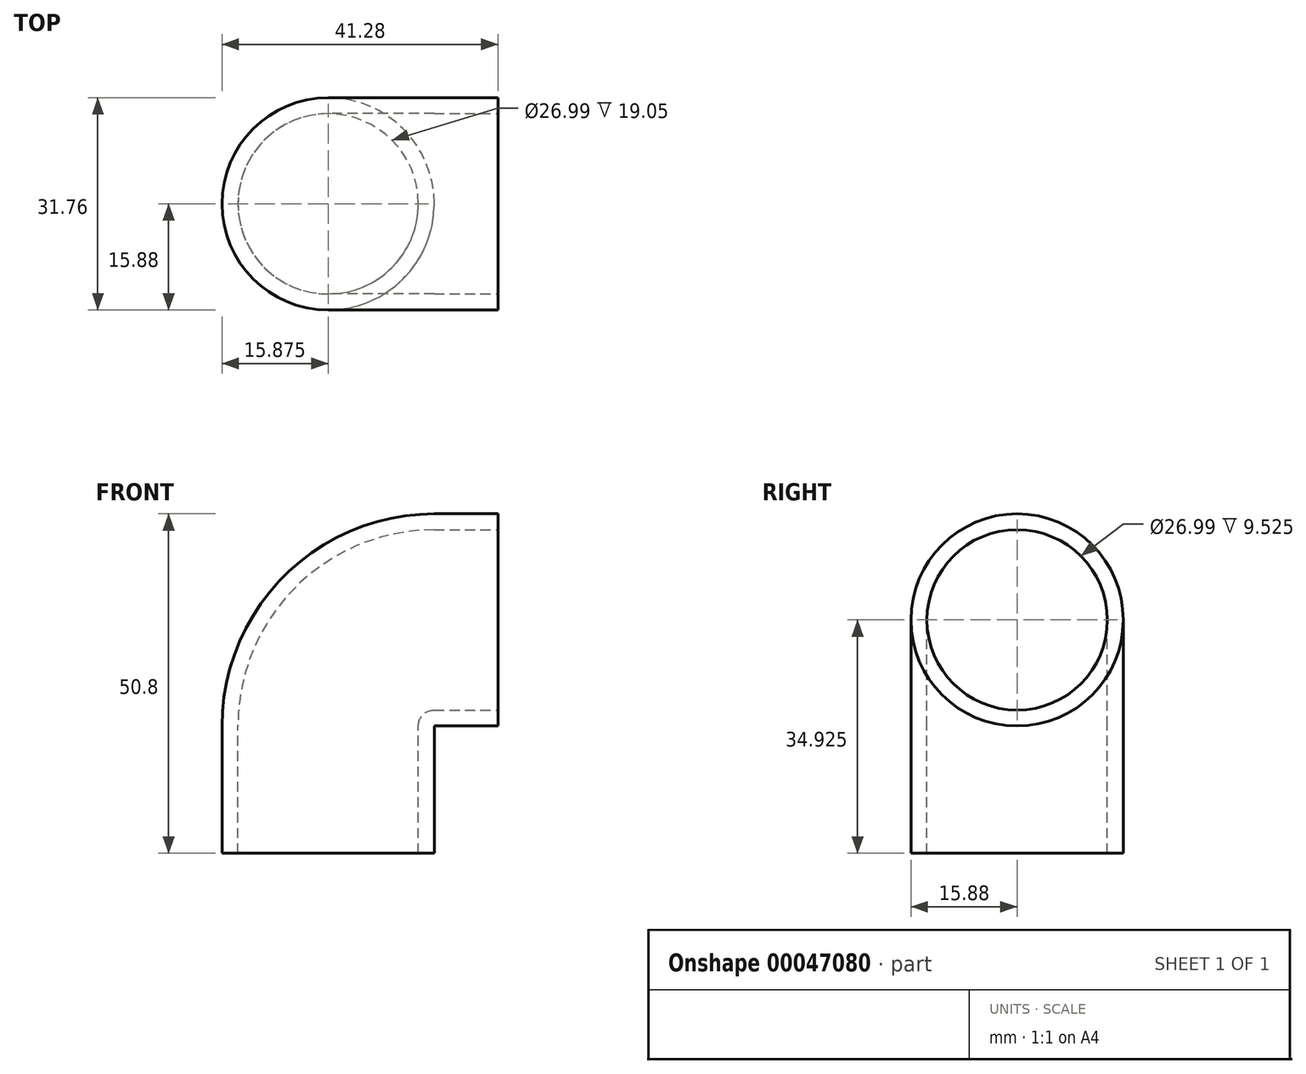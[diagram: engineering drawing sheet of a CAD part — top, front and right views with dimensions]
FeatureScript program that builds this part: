
annotation { "Feature Type Name" : "Feature", "Feature Type Description" : "" }
export const myFeature = defineFeature(function(context is Context, id is Id, definition is map)
    precondition{}
    {
        {
            var Q0;
            Q0=qCreatedBy(makeId("Front.planeOp"),FACE);
            var sketch = newSketch(context, id + "F0", { "sketchPlane" : qUnion([Q0])});
            skLineSegment(sketch, "E0", {"start": v(0, 0) * mm, "end": v(0, 19.05) * mm});
            skLineSegment(sketch, "E1", {"start": v(31.75, 50.8) * mm, "end": v(50.8, 50.8) * mm});
            skPoint(sketch, "E2.visualSharp", {"position": v(0, 50.8) * mm});
            skArc(sketch, "E2.filletArc", {"start": v(31.75, 50.8) * mm, "mid": v(9.3, 41.5) * mm, "end": v(0, 19.05) * mm});
            skSolve(sketch);
        }
        {
            var Q0;
            Q0=qCreatedBy(makeId("Top.planeOp"),FACE);
            var sketch = newSketch(context, id + "F1", { "sketchPlane" : qUnion([Q0])});
            skCircle(sketch, "E3", {"center": v(15.88, 0) * mm, "radius": 15.88 * mm});
            skCircle(sketch, "E4", {"center": v(15.88, 0) * mm, "radius": 13.5 * mm});
            skSolve(sketch);
        }
        {
            var Q0;
            Q0=makeQuery(id+"F1.imprint","IMPRINT",FACE,{"disambiguationData":[TD([[makeQuery(id+"F1.imprint","IMPRINT",EDGE,{"derivedFrom":sQuery(id+"F1.wireOp",EDGE,"E3")}),1.0]])]});
            var Q1;
            Q1=sQuery(id+"F0.wireOp",EDGE,"E0");
            var Q2;
            Q2=sQuery(id+"F0.wireOp",EDGE,"E2.filletArc");
            var Q3;
            Q3=sQuery(id+"F0.wireOp",EDGE,"E1");
            sweep(context, id + "F2", {"profiles" : qUnion([Q0]), "path" : qUnion([Q1, Q2, Q3])});
        }
        {
            var Q0;
            Q0=makeQuery(id+"F2.opSweep","CAP_FACE",FACE,{"disambiguationData":[OSD([sQuery(id+"F0.wireOp",VERTEX,"E1.end"),sQuery(id+"F1.wireOp",EDGE,"E3"),sQuery(id+"F1.wireOp",EDGE,"E4")])],"isStart":false});
            var sketch = newSketch(context, id + "F3", { "sketchPlane" : qUnion([Q0])});
            skCircle(sketch, "E5", {"center": v(0, 34.93) * mm, "radius": 15.95 * mm});
            skSolve(sketch);
        }
        {
            var Q0;
            Q0 = qSketchRegion(id + "F3", true);
            extrude(context, id + "F4", {"entities" : qUnion([Q0]), "operationType" : NewBodyOperationType.REMOVE, "oppositeDirection" : true, "depth" : 9.52 * mm});
        }
    });
